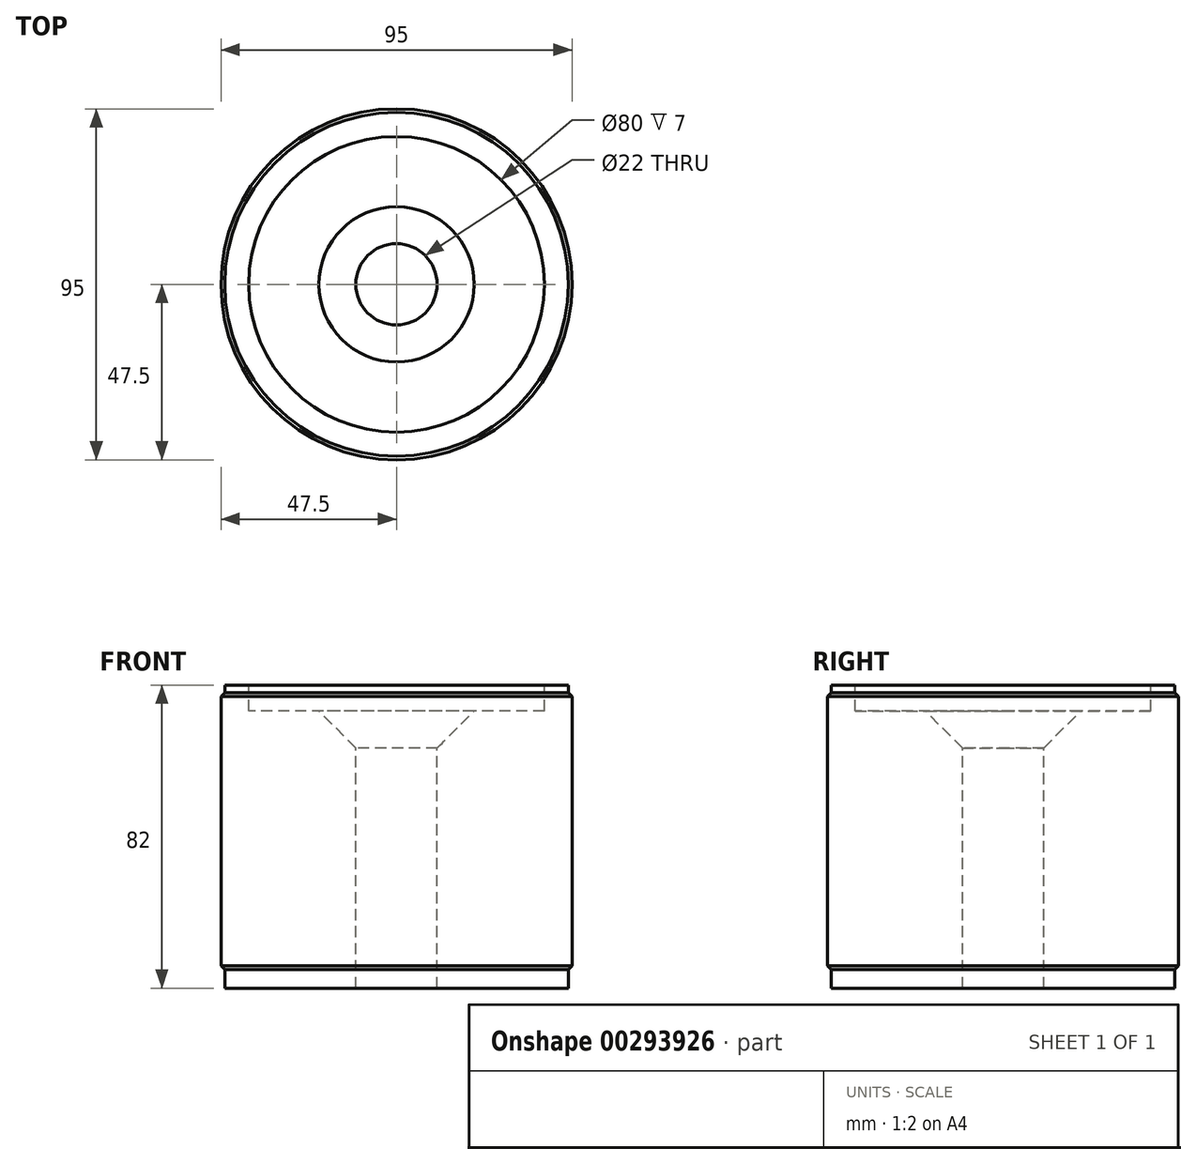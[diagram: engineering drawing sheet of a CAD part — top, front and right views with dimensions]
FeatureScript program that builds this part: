
annotation { "Feature Type Name" : "Feature", "Feature Type Description" : "" }
export const myFeature = defineFeature(function(context is Context, id is Id, definition is map)
    precondition{}
    {
        {
            var Q0;
            Q0=qCreatedBy(makeId("Top.planeOp"),FACE);
            var sketch = newSketch(context, id + "F0", { "sketchPlane" : qUnion([Q0])});
            skCircle(sketch, "E0", {"center": v(0, 0) * mm, "radius": 47.5 * mm});
            skSolve(sketch);
        }
        {
            var Q0;
            Q0=makeQuery(id+"F0.imprint","IMPRINT",FACE,{"disambiguationData":[TD([[makeQuery(id+"F0.imprint","IMPRINT",EDGE,{"derivedFrom":sQuery(id+"F0.wireOp",EDGE,"E0")}),1.0]])]});
            var Q1;
            Q1=sQuery(id+"F0.wireOp",EDGE,"E0");
            extrude(context, id + "F1", {"entities" : qUnion([Q0]), "surfaceEntities" : qUnion([Q1]), "depth" : 75 * mm});
        }
        {
            var Q0;
            Q0=makeQuery(id+"F1.opExtrude","CAP_FACE",FACE,{"disambiguationData":[OSD([sQuery(id+"F0.wireOp",EDGE,"E0")])],"isStart":false});
            var sketch = newSketch(context, id + "F2", { "sketchPlane" : qUnion([Q0])});
            skCircle(sketch, "E1", {"center": v(0, 0) * mm, "radius": 40 * mm});
            skSolve(sketch);
        }
        {
            var Q0;
            Q0=makeQuery(id+"F2.imprint","IMPRINT",FACE,{"disambiguationData":[TD([[makeQuery(id+"F2.imprint","IMPRINT",EDGE,{"derivedFrom":sQuery(id+"F2.wireOp",EDGE,"E1")}),1.0]])]});
            extrude(context, id + "F3", {"entities" : qUnion([Q0]), "operationType" : NewBodyOperationType.REMOVE, "oppositeDirection" : true, "depth" : 5 * mm});
        }
        {
            var Q0;
            Q0=makeQuery(id+"F3.boolean.opBoolean","COPY",FACE,{"derivedFrom":makeQuery(id+"F3.opExtrude","CAP_FACE",FACE,{"disambiguationData":[OSD([sQuery(id+"F2.wireOp",EDGE,"E1")])],"isStart":false})});
            var sketch = newSketch(context, id + "F4", { "sketchPlane" : qUnion([Q0])});
            skPoint(sketch, "E2", {"position": v(0, 0) * mm});
            skSolve(sketch);
        }
        {
            var Q0;
            Q0=sQuery(id+"F4.wireOp",VERTEX,"E2");
            var Q1;
            Q1=makeQuery(id+"F1.opExtrude","SWEPT_BODY",BODY,{"disambiguationData":[OSD([sQuery(id+"F0.wireOp",EDGE,"E0")])]});
            hole(context, id + "F5", {"style" : HoleStyle.C_SINK, "endStyle" : HoleEndStyle.THROUGH, "standardTappedOrClearance" : lookupTablePath({ "standard" : "ISO", "fit" : "Normal", "engagement" : "75%", "pitch" : "1.5 mm", "size" : "M20", "type" : "Clearance" }), "standardBlindInLast" : lookupTablePath({ "fit" : "Standard", "standard" : "ISO", "engagement" : "75%", "pitch" : "1.5 mm", "size" : "M20", "type" : "Clearance" }), "holeDiameter" : 22 * mm, "cSinkDiameter" : 42 * mm, "cSinkAngle" : 90 * degree, "showTappedDepth" : true, "tappedDepth" : 20.5 * mm, "tapClearance" : 3, "locations" : qUnion([Q0]), "scope" : qUnion([Q1])});
        }
        {
            var Q0;
            Q0=makeQuery(id+"F1.opExtrude","SWEPT_FACE",FACE,{"disambiguationData":[OSD([sQuery(id+"F0.wireOp",EDGE,"E0")])]});
            var Q1;
            Q1=makeQuery(id+"F3.boolean.opBoolean","COPY",EDGE,{"derivedFrom":makeQuery(id+"F3.opExtrude","CAP_EDGE",EDGE,{"disambiguationData":[OSD([sQuery(id+"F2.wireOp",EDGE,"E1")])],"isStart":true})});
            var Q2;
            Q2=makeQuery(id+"F5.hole-0.boolean.opBoolean","INTERSECT",EDGE,{"derivedFrom":[makeQuery(id+"F1.opExtrude","CAP_FACE",FACE,{"disambiguationData":[OSD([sQuery(id+"F0.wireOp",EDGE,"E0")])],"isStart":true}),makeQuery(id+"F5.hole-0.opRevolve","SWEPT_FACE",FACE,{"disambiguationData":[OSD([sQuery(id+"F5.hole-0.sketch.wireOp",EDGE,"core_line_2")])]})]});
            chamfer(context, id + "F6", {"entities" : qUnion([Q0, Q1, Q2]), "width" : 1 * mm, "tangentPropagation" : true});
        }
        {
            var Q0;
            Q0=makeQuery(id+"F1.opExtrude","CAP_FACE",FACE,{"disambiguationData":[OSD([sQuery(id+"F0.wireOp",EDGE,"E0")])],"isStart":true});
            extrude(context, id + "F7", {"entities" : qUnion([Q0]), "operationType" : NewBodyOperationType.ADD, "depth" : 5 * mm});
        }
        {
            var Q0;
            Q0=makeQuery(id+"F1.opExtrude","CAP_FACE",FACE,{"disambiguationData":[OSD([sQuery(id+"F0.wireOp",EDGE,"E0")])],"isStart":false});
            extrude(context, id + "F8", {"entities" : qUnion([Q0]), "operationType" : NewBodyOperationType.ADD, "depth" : 2 * mm});
        }
    });
